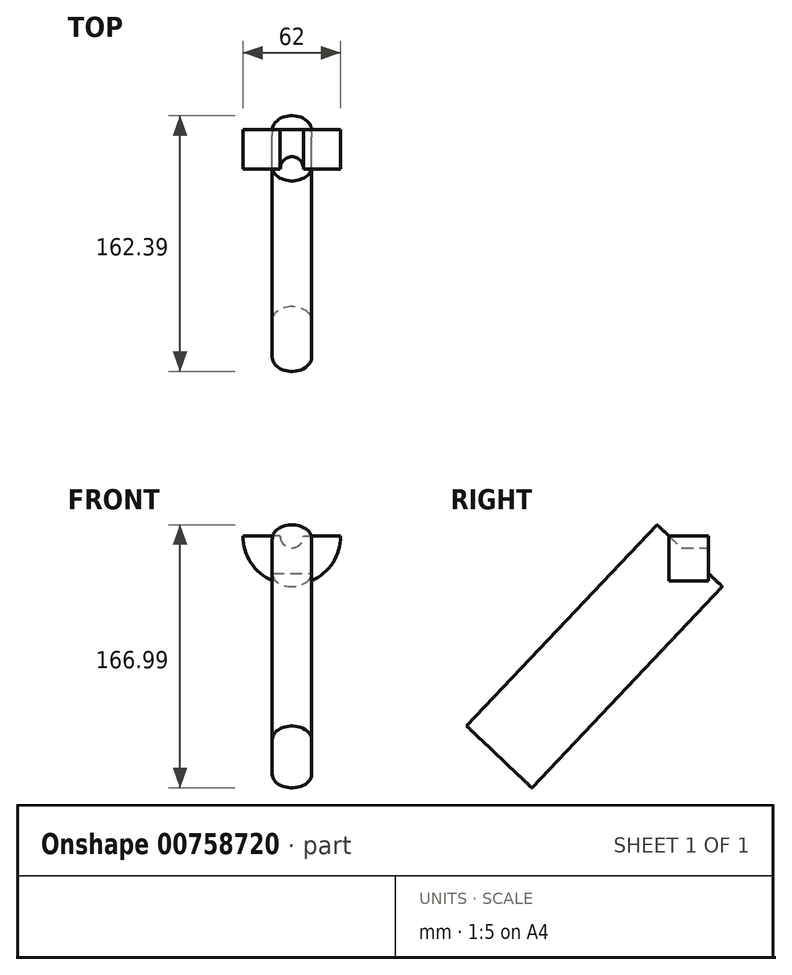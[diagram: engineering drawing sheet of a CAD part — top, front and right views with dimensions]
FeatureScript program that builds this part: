
annotation { "Feature Type Name" : "Feature", "Feature Type Description" : "" }
export const myFeature = defineFeature(function(context is Context, id is Id, definition is map)
    precondition{}
    {
        {
            var Q0;
            Q0=qCreatedBy(makeId("Front.planeOp"),FACE);
            var sketch = newSketch(context, id + "F0", { "sketchPlane" : qUnion([Q0])});
            skCircle(sketch, "E0", {"center": v(0, 0) * mm, "radius": 31 * mm});
            skCircle(sketch, "E1", {"center": v(0, 0) * mm, "radius": 7.5 * mm});
            skLineSegment(sketch, "E2", {"start": v(0, 0) * mm, "end": v(-31, 0) * mm});
            skLineSegment(sketch, "E3", {"start": v(0, 0) * mm, "end": v(31, 0) * mm});
            skSolve(sketch);
        }
        {
            var Q0;
            {var subQ0=sQuery(id+"F0.wireOp",EDGE,"E2");var subQ1=sQuery(id+"F0.wireOp",EDGE,"E0");var subQ2=makeQuery(id+"F0.imprint","INTERSECT",VERTEX,{"derivedFrom":[subQ1,subQ0]});Q0=makeQuery(id+"F0.imprint","IMPRINT",FACE,{"disambiguationData":[TD([[makeQuery(id+"F0.imprint","IMPRINT",EDGE,{"disambiguationData":[TD([[subQ2,-1.0]])],"derivedFrom":subQ1}),1.0]])]});}
            extrude(context, id + "F1", {"entities" : qUnion([Q0]), "depth" : 25 * mm, "offsetDistance" : 25 * mm});
        }
        {
            var Q0;
            Q0=qCreatedBy(makeId("Right.planeOp"),FACE);
            var sketch = newSketch(context, id + "F2", { "sketchPlane" : qUnion([Q0])});
            skLineSegment(sketch, "E4", {"start": v(0, 0) * mm, "end": v(6.92, -30.22) * mm});
            skLineSegment(sketch, "E5", {"start": v(6.92, -30.22) * mm, "end": v(6.92, -30.22) * mm});
            skLineSegment(sketch, "E6", {"start": v(6.92, -30.22) * mm, "end": v(-25, 0) * mm});
            skSolve(sketch);
        }
        {
            var Q0;
            Q0=sQuery(id+"F2.wireOp",EDGE,"E6");
            cPlane(context, id + "F3", {"entities" : qUnion([Q0]), "cplaneType" : CPlaneType.LINE_ANGLE, "offset" : 25 * mm, "angle" : 0 * degree, "flipAlignment" : true, "width" : 150 * mm, "height" : 150 * mm});
        }
        {
            var Q0;
            Q0=qCreatedBy(id+"F3.planeOp",FACE);
            var sketch = newSketch(context, id + "F4", { "sketchPlane" : qUnion([Q0])});
            skLineSegment(sketch, "E7", {"start": v(0, 0) * mm, "end": v(0, 16) * mm});
            skLineSegment(sketch, "E8", {"start": v(0, 0) * mm, "end": v(0, -16) * mm});
            skCircle(sketch, "E9", {"center": v(0, -16) * mm, "radius": 12.5 * mm});
            skCircle(sketch, "E10", {"center": v(0, 16) * mm, "radius": 12.5 * mm});
            skLineSegment(sketch, "E11", {"start": v(0, 16) * mm, "end": v(12.5, 16) * mm});
            skLineSegment(sketch, "E12", {"start": v(12.5, 16) * mm, "end": v(12.5, -16) * mm});
            skLineSegment(sketch, "E13", {"start": v(12.5, -16) * mm, "end": v(0, -16) * mm});
            skLineSegment(sketch, "E14", {"start": v(-12.5, -16) * mm, "end": v(-12.5, 16) * mm});
            skLineSegment(sketch, "E15", {"start": v(-12.5, 16) * mm, "end": v(0, 16) * mm});
            skSolve(sketch);
        }
        {
            var Q0;
            {var subQ0=sQuery(id+"F4.wireOp",EDGE,"E11");Q0=makeQuery(id+"F4.imprint","IMPRINT",FACE,{"disambiguationData":[TD([[makeQuery(id+"F4.imprint","IMPRINT",EDGE,{"derivedFrom":subQ0}),1.0]])]});}
            var Q1;
            {var subQ0=sQuery(id+"F4.wireOp",EDGE,"E11");Q1=makeQuery(id+"F4.imprint","IMPRINT",FACE,{"disambiguationData":[TD([[makeQuery(id+"F4.imprint","IMPRINT",EDGE,{"derivedFrom":subQ0}),-1.0]])]});}
            var Q2;
            {var subQ0=sQuery(id+"F4.wireOp",EDGE,"E15");Q2=makeQuery(id+"F4.imprint","IMPRINT",FACE,{"disambiguationData":[TD([[makeQuery(id+"F4.imprint","IMPRINT",EDGE,{"derivedFrom":subQ0}),-1.0]])]});}
            var Q3;
            {var subQ0=sQuery(id+"F4.wireOp",EDGE,"E13");Q3=makeQuery(id+"F4.imprint","IMPRINT",FACE,{"disambiguationData":[TD([[makeQuery(id+"F4.imprint","IMPRINT",EDGE,{"derivedFrom":subQ0}),1.0]])]});}
            var Q4;
            {var subQ0=sQuery(id+"F4.wireOp",EDGE,"E12");Q4=makeQuery(id+"F4.imprint","IMPRINT",FACE,{"disambiguationData":[TD([[makeQuery(id+"F4.imprint","IMPRINT",EDGE,{"derivedFrom":subQ0}),-1.0]])]});}
            var Q5;
            {var subQ0=sQuery(id+"F4.wireOp",EDGE,"E14");Q5=makeQuery(id+"F4.imprint","IMPRINT",FACE,{"disambiguationData":[TD([[makeQuery(id+"F4.imprint","IMPRINT",EDGE,{"derivedFrom":subQ0}),-1.0]])]});}
            var Q6;
            {var subQ0=sQuery(id+"F4.wireOp",EDGE,"E13");Q6=makeQuery(id+"F4.imprint","IMPRINT",FACE,{"disambiguationData":[TD([[makeQuery(id+"F4.imprint","IMPRINT",EDGE,{"derivedFrom":subQ0}),-1.0]])]});}
            extrude(context, id + "F5", {"entities" : qUnion([Q0, Q1, Q2, Q3, Q4, Q5, Q6]), "operationType" : NewBodyOperationType.ADD, "depth" : 176 * mm, "offsetDistance" : 25 * mm});
        }
    });
